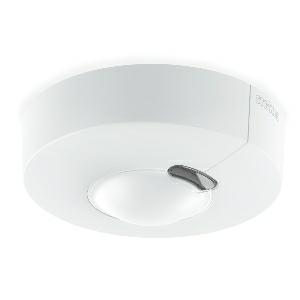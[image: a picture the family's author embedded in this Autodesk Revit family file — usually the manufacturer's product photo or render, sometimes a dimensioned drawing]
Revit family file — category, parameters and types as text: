
# Revit family: hf_3360_058234
name_source: partatom
category: Elektroinstallationen
revit_build: Autodesk Revit 2016 (Build: 20190508_0715(x64)
units: mm (PartAtom-declared; Revit-internal decimal feet)

## family parameters
Basisbauteil = Fläche
Beim Laden mit Abzugskörper schneiden = Nein
Bemaßung runder Anschluss = Durchmesser verwenden
Beschriftungsausrichtung beibehalten = Nein
Gemeinsam genutzt = Nein
Raumberechnungspunkt = Nein
Teiletyp = Normal

## types (1)
- HF 3360
    Apparent Load = 0 VA
    Beschreibung = Type: Motion detectors; Dimensions (Ø x H): 126 x 52 mm; Sensor Technology: High frequency; Application, place: Indoors; Application, room: function room / ancillary room, stairwell, WC / washroom, multi-storey / underground car park, Indoors; Installation site: wall, ceiling, corner; Installation: Surface wiring; HF-system: 5,8 GHz; Mounting height: 2,00 – 4,00 m; Optimum mounting height: 2,8 m; Detection angle: 360 °; Sneak-by guard: Yes; Twilight setting TEACH: Yes; Time setting: 0 sec – 1092 min; Basic light level function: Yes; KNX functions: Photo-cell controller, Basic light level function, Light level, HVAC output, Constant-lighting control, Light output 2x, Presence output, Day / night function; With bus coupling: Yes; Settings via: ETS software, Remote control, Bus, Smart Remote; IP-rating: IP54; Material: Plastic; Colour: white; Colour, RAL: 9003; Version: KNX - surface, rd.; PU1, EAN: 4007841058234
    Height = 0 mm  [stored 0 ft]
    Hersteller = Steinel
    Length = 126 mm
    ModVariant = Nein
    Modell = 058234
    Mounting Type = Surface mounted
    Number of Poles = 1
    OnlyDefault = Ja
    Power Factor = 1
    Product Name = HF 3360
    Product group = Sensor-switched indoor light
    ProductGroupID = 30
    Protection Class = Protection class
    Protection Degree = IP 54
    RlxData = <blob elided: 36465 chars, md5=f1a45614>
    SensorDataFile = {"IESDataFiles":[]}
    Typenbild = produkt1_058234.jpg
    Typenkommentare = Product without accessories
    URL = http://relux.com
    VarID = ---
    Voltage = 0 V
    Vorgabe-Ansicht = 1800 mm
    Weight = 0.00 kg
    Width = 0 mm  [stored 0 ft]

note: [stored X ft] marks values corroborated as IEEE doubles in the binary element streams (Revit-internal decimal feet)

## geometry (parser evidence)
native form markers: Sweep x10
no freeform markers — native parametric forms only
